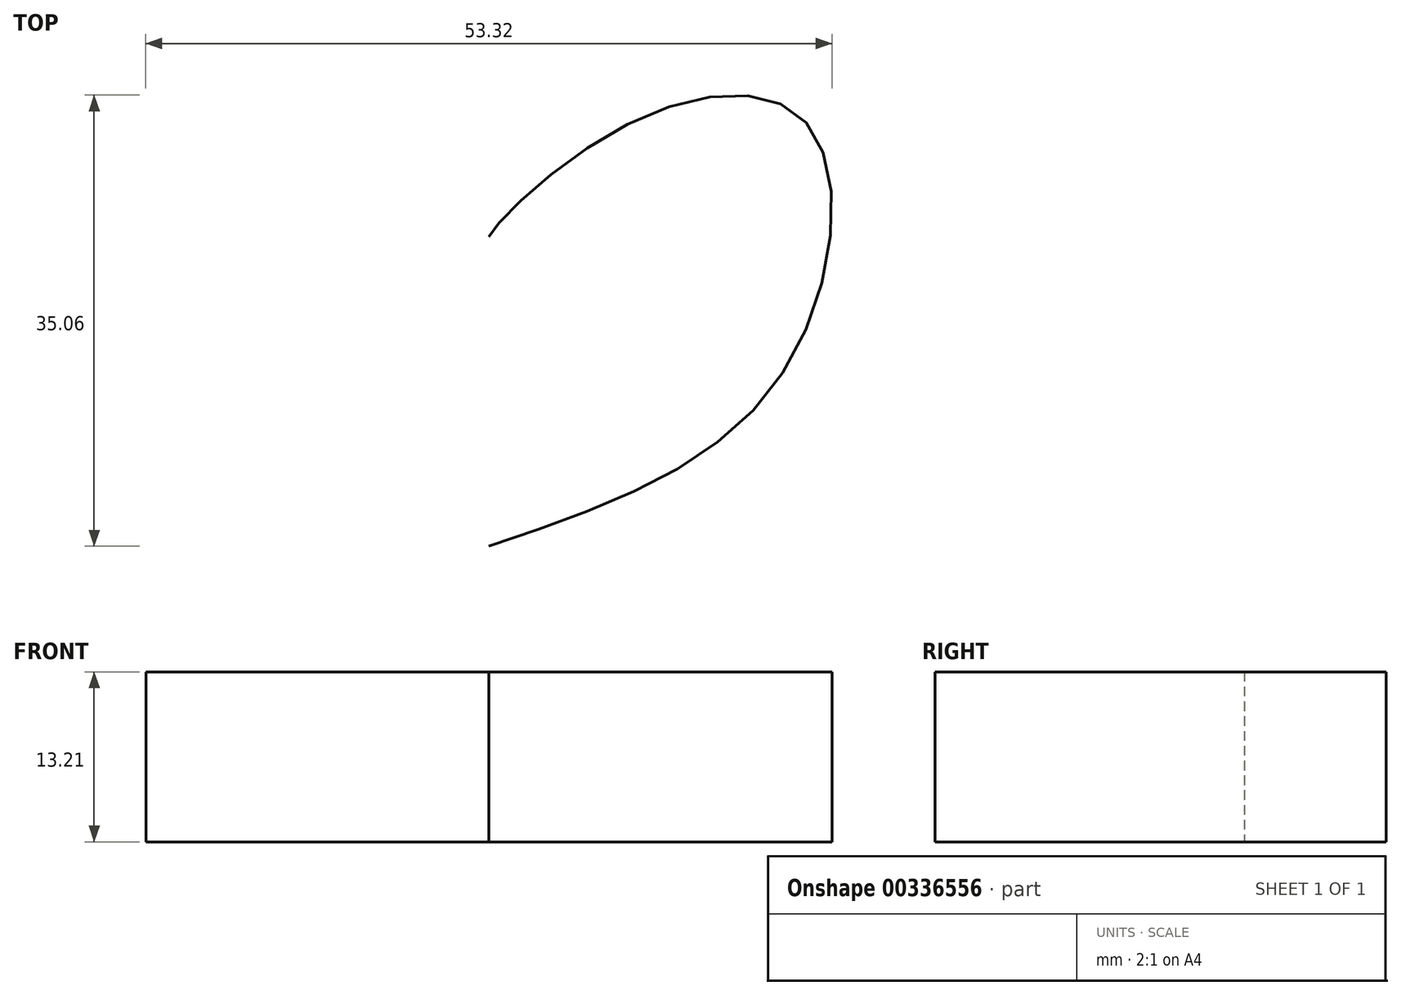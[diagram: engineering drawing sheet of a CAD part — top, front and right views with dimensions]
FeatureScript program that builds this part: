
annotation { "Feature Type Name" : "Feature", "Feature Type Description" : "" }
export const myFeature = defineFeature(function(context is Context, id is Id, definition is map)
    precondition{}
    {
        {
            var Q0;
            Q0=qCreatedBy(makeId("Top.planeOp"),FACE);
            var sketch = newSketch(context, id + "F0", { "sketchPlane" : qUnion([Q0])});
            skFitSpline(sketch, "E0", {"points": [v(0, -28.18) * mm, v(-22.66, -14.98) * mm, v(-24.83, 4.53) * mm, v(-11.04, 4.73) * mm, v(0, -4.14) * mm, v(0, -4.53) * mm], "startDerivative": vector(-92.1, 31.14) * mm, "endDerivative": vector(-3.58, -8.14) * mm});
            skFitSpline(sketch, "E1.MirrorCS", {"points": [v(0, -28.18) * mm, v(22.66, -14.98) * mm, v(24.83, 4.53) * mm, v(11.04, 4.73) * mm, v(0, -4.14) * mm, v(0, -4.53) * mm], "startDerivative": vector(92.1, 31.14) * mm, "endDerivative": vector(3.58, -8.14) * mm});
            skSolve(sketch);
        }
        {
            var Q0;
            Q0 = qSketchRegion(id + "F0", true);
            extrude(context, id + "F1", {"entities" : qUnion([Q0]), "depth" : 13.2 * mm});
        }
    });
